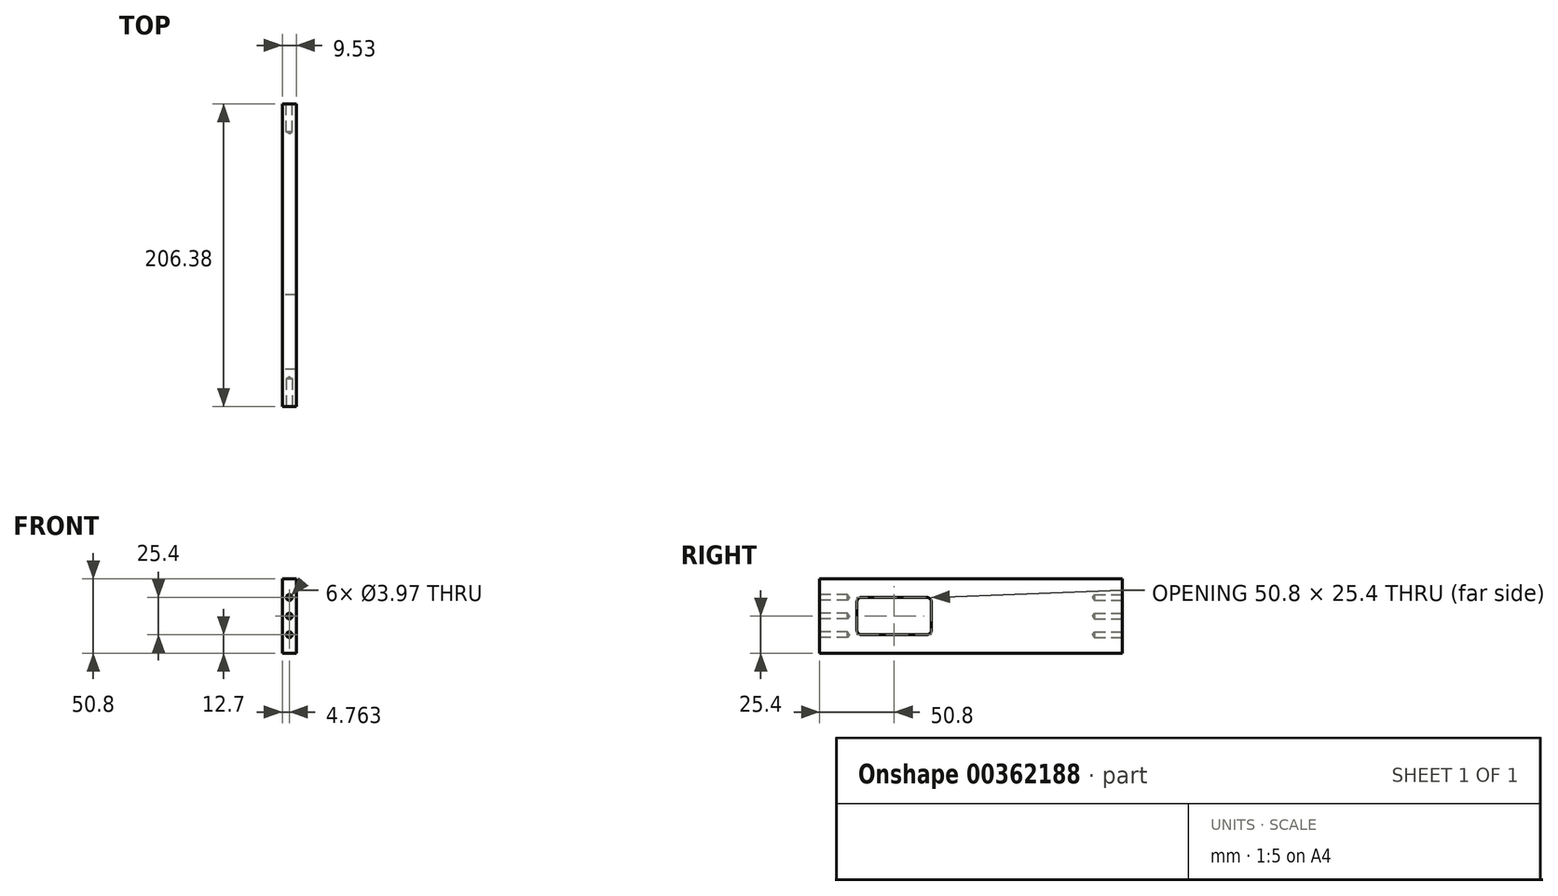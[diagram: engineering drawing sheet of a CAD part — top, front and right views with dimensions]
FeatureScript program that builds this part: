
annotation { "Feature Type Name" : "Feature", "Feature Type Description" : "" }
export const myFeature = defineFeature(function(context is Context, id is Id, definition is map)
    precondition{}
    {
        {
            var Q0;
            Q0=qCreatedBy(makeId("Right.planeOp"),FACE);
            var sketch = newSketch(context, id + "F0", { "sketchPlane" : qUnion([Q0])});
            skLineSegment(sketch, "E0.bottom", {"start": v(0, 0) * mm, "end": v(206.38, 0) * mm});
            skLineSegment(sketch, "E0.top", {"start": v(0, 50.8) * mm, "end": v(206.38, 50.8) * mm});
            skLineSegment(sketch, "E0.left", {"start": v(0, 0) * mm, "end": v(0, 50.8) * mm});
            skLineSegment(sketch, "E0.right", {"start": v(206.38, 0) * mm, "end": v(206.38, 50.8) * mm});
            skLineSegment(sketch, "E1.bottom", {"start": v(25.4, 38.1) * mm, "end": v(76.2, 38.1) * mm});
            skLineSegment(sketch, "E1.top", {"start": v(25.4, 12.7) * mm, "end": v(76.2, 12.7) * mm});
            skLineSegment(sketch, "E1.left", {"start": v(25.4, 38.1) * mm, "end": v(25.4, 12.7) * mm});
            skLineSegment(sketch, "E1.right", {"start": v(76.2, 38.1) * mm, "end": v(76.2, 12.7) * mm});
            skLineSegment(sketch, "E2", {"start": v(76.2, 38.1) * mm, "end": v(76.2, 50.8) * mm, "construction": true});
            skLineSegment(sketch, "E3", {"start": v(25.4, 12.7) * mm, "end": v(25.4, 0) * mm, "construction": true});
            skLineSegment(sketch, "E4", {"start": v(25.4, 12.7) * mm, "end": v(0, 12.7) * mm, "construction": true});
            skSolve(sketch);
        }
        {
            var Q0;
            Q0=makeQuery(id+"F0.imprint","IMPRINT",FACE,{"disambiguationData":[TD([[makeQuery(id+"F0.imprint","IMPRINT",EDGE,{"derivedFrom":sQuery(id+"F0.wireOp",EDGE,"E0.bottom")}),1.0]])]});
            extrude(context, id + "F1", {"entities" : qUnion([Q0]), "depth" : 9.52 * mm});
        }
        {
            var Q0;
            Q0=makeQuery(id+"F1.opExtrude","SWEPT_FACE",FACE,{"disambiguationData":[OSD([sQuery(id+"F0.wireOp",EDGE,"E0.right")])]});
            var sketch = newSketch(context, id + "F2", { "sketchPlane" : qUnion([Q0])});
            skLineSegment(sketch, "E5", {"start": v(0, 25.4) * mm, "end": v(-9.53, 25.4) * mm, "construction": true});
            skLineSegment(sketch, "E6", {"start": v(-4.76, 25.4) * mm, "end": v(-4.76, 50.8) * mm, "construction": true});
            skLineSegment(sketch, "E7", {"start": v(-4.76, 0) * mm, "end": v(-4.76, 25.4) * mm, "construction": true});
            skPoint(sketch, "E8", {"position": v(-4.76, 38.1) * mm});
            skPoint(sketch, "E9", {"position": v(-4.76, 25.4) * mm});
            skPoint(sketch, "E10", {"position": v(-4.76, 12.7) * mm});
            skSolve(sketch);
        }
        {
            var Q0;
            Q0=sQuery(id+"F2.wireOp",VERTEX,"E8");
            var Q1;
            Q1=sQuery(id+"F2.wireOp",VERTEX,"E9");
            var Q2;
            Q2=sQuery(id+"F2.wireOp",VERTEX,"E10");
            var Q3;
            Q3=makeQuery(id+"F1.opExtrude","SWEPT_BODY",BODY,{"disambiguationData":[OSD([sQuery(id+"F0.wireOp",EDGE,"E0.bottom"),sQuery(id+"F0.wireOp",EDGE,"E0.top"),sQuery(id+"F0.wireOp",EDGE,"E0.left"),sQuery(id+"F0.wireOp",EDGE,"E0.right")])]});
            hole(context, id + "F3", {"style" : HoleStyle.SIMPLE, "endStyle" : HoleEndStyle.BLIND, "holeDiameter" : 3.97 * mm, "holeDepth" : 19.05 * mm, "isTappedThrough" : true, "tappedDepth" : 12.7 * mm, "tapClearance" : 3, "startFromSketch" : true, "locations" : qUnion([Q0, Q1, Q2]), "scope" : qUnion([Q3])});
        }
        {
            var Q0;
            Q0=makeQuery(id+"F1.opExtrude","SWEPT_FACE",FACE,{"disambiguationData":[OSD([sQuery(id+"F0.wireOp",EDGE,"E0.left")])]});
            var sketch = newSketch(context, id + "F4", { "sketchPlane" : qUnion([Q0])});
            skLineSegment(sketch, "E11", {"start": v(9.53, 25.4) * mm, "end": v(0, 25.4) * mm, "construction": true});
            skLineSegment(sketch, "E12", {"start": v(4.76, 0) * mm, "end": v(4.76, 25.4) * mm, "construction": true});
            skLineSegment(sketch, "E13", {"start": v(4.76, 25.4) * mm, "end": v(4.76, 50.8) * mm, "construction": true});
            skPoint(sketch, "E14", {"position": v(4.76, 38.1) * mm});
            skPoint(sketch, "E15", {"position": v(4.76, 25.4) * mm});
            skPoint(sketch, "E16", {"position": v(4.76, 12.7) * mm});
            skSolve(sketch);
        }
        {
            var Q0;
            Q0=sQuery(id+"F4.wireOp",VERTEX,"E14");
            var Q1;
            Q1=sQuery(id+"F4.wireOp",VERTEX,"E15");
            var Q2;
            Q2=sQuery(id+"F4.wireOp",VERTEX,"E16");
            var Q3;
            Q3=makeQuery(id+"F1.opExtrude","SWEPT_BODY",BODY,{"disambiguationData":[OSD([sQuery(id+"F0.wireOp",EDGE,"E0.bottom"),sQuery(id+"F0.wireOp",EDGE,"E0.top"),sQuery(id+"F0.wireOp",EDGE,"E0.left"),sQuery(id+"F0.wireOp",EDGE,"E0.right")])]});
            hole(context, id + "F5", {"style" : HoleStyle.SIMPLE, "endStyle" : HoleEndStyle.BLIND, "holeDiameter" : 3.97 * mm, "holeDepth" : 19.05 * mm, "isTappedThrough" : true, "tappedDepth" : 12.7 * mm, "tapClearance" : 3, "startFromSketch" : true, "locations" : qUnion([Q0, Q1, Q2]), "scope" : qUnion([Q3])});
        }
        {
            var Q0;
            Q0=makeQuery(id+"F1.opExtrude","SWEPT_EDGE",EDGE,{"disambiguationData":[OSD([sQuery(id+"F0.wireOp",EDGE,"E1.bottom"),sQuery(id+"F0.wireOp",EDGE,"E1.right")])]});
            var Q1;
            Q1=makeQuery(id+"F1.opExtrude","SWEPT_EDGE",EDGE,{"disambiguationData":[OSD([sQuery(id+"F0.wireOp",EDGE,"E1.bottom"),sQuery(id+"F0.wireOp",EDGE,"E1.left")])]});
            var Q2;
            Q2=makeQuery(id+"F1.opExtrude","SWEPT_EDGE",EDGE,{"disambiguationData":[OSD([sQuery(id+"F0.wireOp",EDGE,"E1.top"),sQuery(id+"F0.wireOp",EDGE,"E1.left")])]});
            var Q3;
            Q3=makeQuery(id+"F1.opExtrude","SWEPT_EDGE",EDGE,{"disambiguationData":[OSD([sQuery(id+"F0.wireOp",EDGE,"E1.top"),sQuery(id+"F0.wireOp",EDGE,"E1.right")])]});
            fillet(context, id + "F6", {"entities" : qUnion([Q0, Q1, Q2, Q3]), "radius" : 3.17 * mm, "tangentPropagation" : true, "allowEdgeOverflow" : false});
        }
    });
